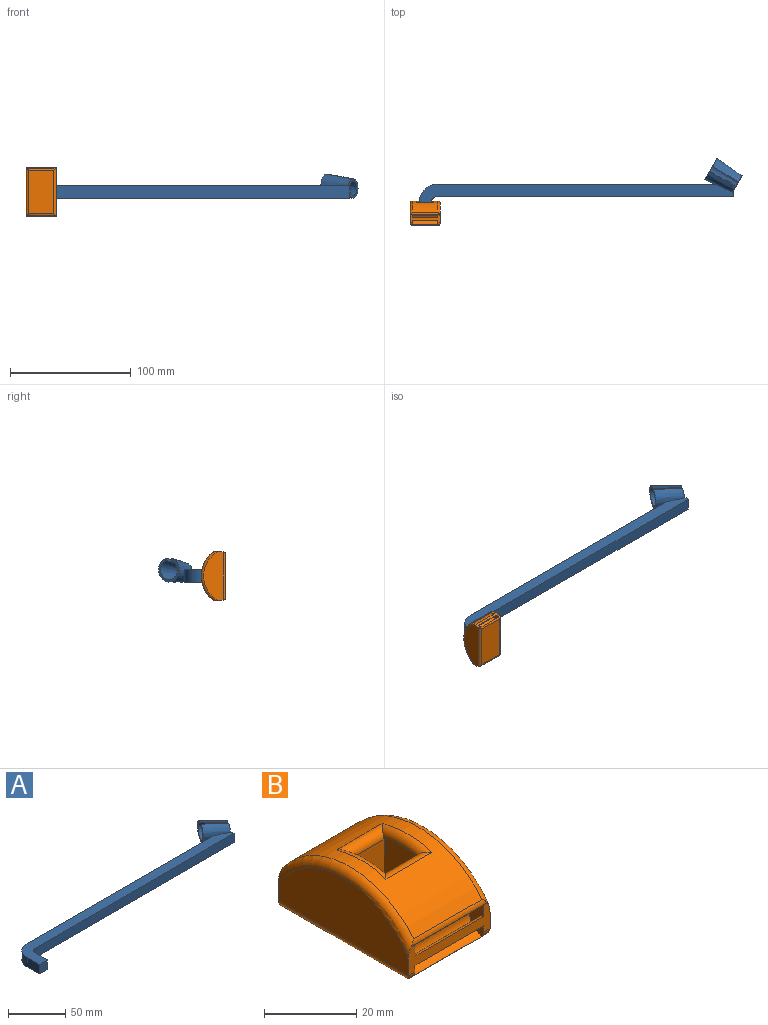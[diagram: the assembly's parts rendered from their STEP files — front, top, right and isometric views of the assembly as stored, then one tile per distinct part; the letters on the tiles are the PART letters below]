
ASSEMBLY  parts=2 mates=1
PART A: 21 faces, bbox 267.1x51.5x19.8 mm
  f0: plane 8.72x5.06mm, normal (0.5,0.87,0), area 25.3mm2, adj f1,f8,f10,f13
  f1: plane 236.34x10mm, normal (0,1,0), area 2327.8mm2, adj f0,f2,f9,f10,f13
  f2: plane 260.12x30.12mm, normal (0,0,1), area 2705.4mm2, adj f1,f3,f4,f5,f6,f7,f8,f9
  f3: plane 15x10mm, normal (-1,0,0), area 150mm2, adj f2,f4,f9,f10
  f4: plane 10x10mm, normal (0,-1,0), area 100mm2, adj f2,f3,f5,f10
  f5: plane 15x10mm, normal (1,0,0), area 150mm2, adj f2,f4,f6,f10
  f6: cylinder r=5mm len=10mm, axis (0,0,-1), area 78.5mm2, adj f2,f5,f7,f10
  f7: plane 245x10mm, normal (0,-1,0), area 2450mm2, adj f2,f6,f8,f10
  f8: plane 10x5mm, normal (1,0,0), area 50mm2, adj f0,f2,f7,f10,f11,f12
  f9: cylinder r=15mm len=15mm, axis (0,0,-1), area 235.6mm2, adj f1,f2,f3,f10
  f10: plane 260x30mm, normal (0,0,-1), area 2735.4mm2, adj f0,f1,f3,f4,f5,f6,f7,f8
  f11: plane 15.73x12.15mm, normal (0.87,-0.5,0), area 55mm2, adj f8,f13,f14,f16
  f12: plane 7.74x5.39mm, normal (0.87,-0.5,0), area 14.5mm2, adj f2,f8,f13,f14,f17
  f13: bspline ~30.71x28.2mm, area 1186.8mm2, adj f0,f1,f2,f11,f12,f15,f16,f17
  f14: bspline ~28.7x24.71mm, area 971mm2, adj f11,f12,f15,f16,f17,f18,f19,f20
  f15: plane 19.66x17.35mm, normal (-0.87,0.5,0), area 103.7mm2, adj f13,f14,f16,f17
  f16: plane 21.65x13.4mm, normal (-0.46,-0.85,0.26), area 50mm2, adj f11,f13,f14,f15
  f17: plane 22.17x12.5mm, normal (0.5,0.83,0.26), area 50mm2, adj f12,f13,f14,f15
  f18: plane 7.66x3.49mm, normal (0,0,1), area 2.9mm2, adj f14,f19,f20
  f19: plane 4.4x1.86mm, normal (0,1,0), area 6.1mm2, adj f14,f18,f20
  f20: plane 8.66x5mm, normal (0.5,0.87,0), area 34.8mm2, adj f14,f18,f19
PART B: 31 faces, bbox 25x47.1x22.1 mm
  f0: cylinder r=25mm len=39.13mm, axis (1,0,0), area 724.2mm2, adj f19,f20,f21,f22,f23,f24,f25,f26
  f1: plane 25x7.32mm, normal (0,-1,0), area 81.8mm2, adj f2,f3,f6,f7,f8,f13,f23,f25
  f2: plane 40x16mm, normal (-1,0,0), area 504.9mm2, adj f1,f4,f26,f28
  f3: plane 40x16mm, normal (1,0,0), area 504.9mm2, adj f1,f4,f23,f29
  f4: plane 25x7.32mm, normal (0,1,0), area 81.8mm2, adj f2,f3,f9,f10,f11,f12,f23,f24
  f5: plane 36x21mm, normal (0,0,-1), area 756mm2, adj f27,f28,f29,f30
  f6: cylinder r=4.25mm len=21mm, axis (1,0,0), area 271.5mm2, adj f1,f8,f13,f30
  f7: cylinder r=1.25mm len=21mm, axis (1,0,0), area 82.5mm2, adj f1,f8,f13
  f8: plane 8.48x4.25mm, normal (1,0,0), area 25.7mm2, adj f1,f6,f7,f30
  f9: cylinder r=4.25mm len=21mm, axis (1,0,0), area 271.5mm2, adj f4,f11,f12,f27
  f10: cylinder r=1.25mm len=21mm, axis (1,0,0), area 82.5mm2, adj f4,f11,f12
  f11: plane 8.48x4.25mm, normal (1,0,0), area 25.7mm2, adj f4,f9,f10,f27
  f12: plane 8.48x4.25mm, normal (-1,0,0), area 25.7mm2, adj f4,f9,f10,f27
  f13: plane 8.48x4.25mm, normal (-1,0,0), area 25.7mm2, adj f1,f6,f7,f30
  f14: plane 13x10.24mm, normal (-1,0,0), area 129.4mm2, adj f15,f17,f18,f19,f20,f22
  f15: plane 11.89x10.1mm, normal (0,-1,0), area 120.1mm2, adj f14,f16,f18,f22
  f16: plane 13x10.24mm, normal (1,0,0), area 129.4mm2, adj f15,f17,f18,f19,f21,f22
  f17: plane 11.89x10.1mm, normal (0,1,0), area 120.1mm2, adj f14,f16,f18,f19
  f18: plane 10.1x10.1mm, normal (0,0,1), area 102mm2, adj f14,f15,f16,f17
  f19: cylinder r=2mm len=14.1mm, axis (1,0,0), area 42.8mm2, adj f0,f14,f16,f17,f20,f21
  f20: torus R=23mm, axis (-1,0,0), area 39.3mm2, adj f0,f14,f19,f22
  f21: torus R=23mm, axis (-1,0,0), area 39.3mm2, adj f0,f16,f19,f22
  f22: cylinder r=2mm len=14.1mm, axis (1,0,0), area 42.8mm2, adj f0,f14,f15,f16,f20,f21
  f23: torus R=23mm, axis (1,0,0), area 147.2mm2, adj f0,f1,f3,f4,f24,f25
  f24: cylinder r=2mm len=23.41mm, axis (1,0,0), area 29.8mm2, adj f0,f4,f23,f26
  f25: cylinder r=2mm len=23.41mm, axis (1,0,0), area 29.8mm2, adj f0,f1,f23,f26
  f26: torus R=23mm, axis (1,0,0), area 147.2mm2, adj f0,f1,f2,f4,f24,f25
  f27: cylinder r=2mm len=25mm, axis (-1,0,0), area 46.2mm2, adj f4,f5,f9,f11,f12,f28,f29
  f28: cylinder r=2mm len=40mm, axis (0,-1,0), area 121.1mm2, adj f2,f5,f27,f30
  f29: cylinder r=2mm len=40mm, axis (0,1,0), area 121.1mm2, adj f3,f5,f27,f30
  f30: cylinder r=2mm len=25mm, axis (1,0,0), area 46.2mm2, adj f1,f5,f6,f8,f13,f28,f29
PLACE A t=(-5.05,-1.09,0)mm
PLACE B rot(axis=(-1,0,0),90deg) t=(0,-5,0)mm
MATE fastened A.f3 <-> B.f16  axis (-1,0,0) through (-5.05,6.41,0)mm
